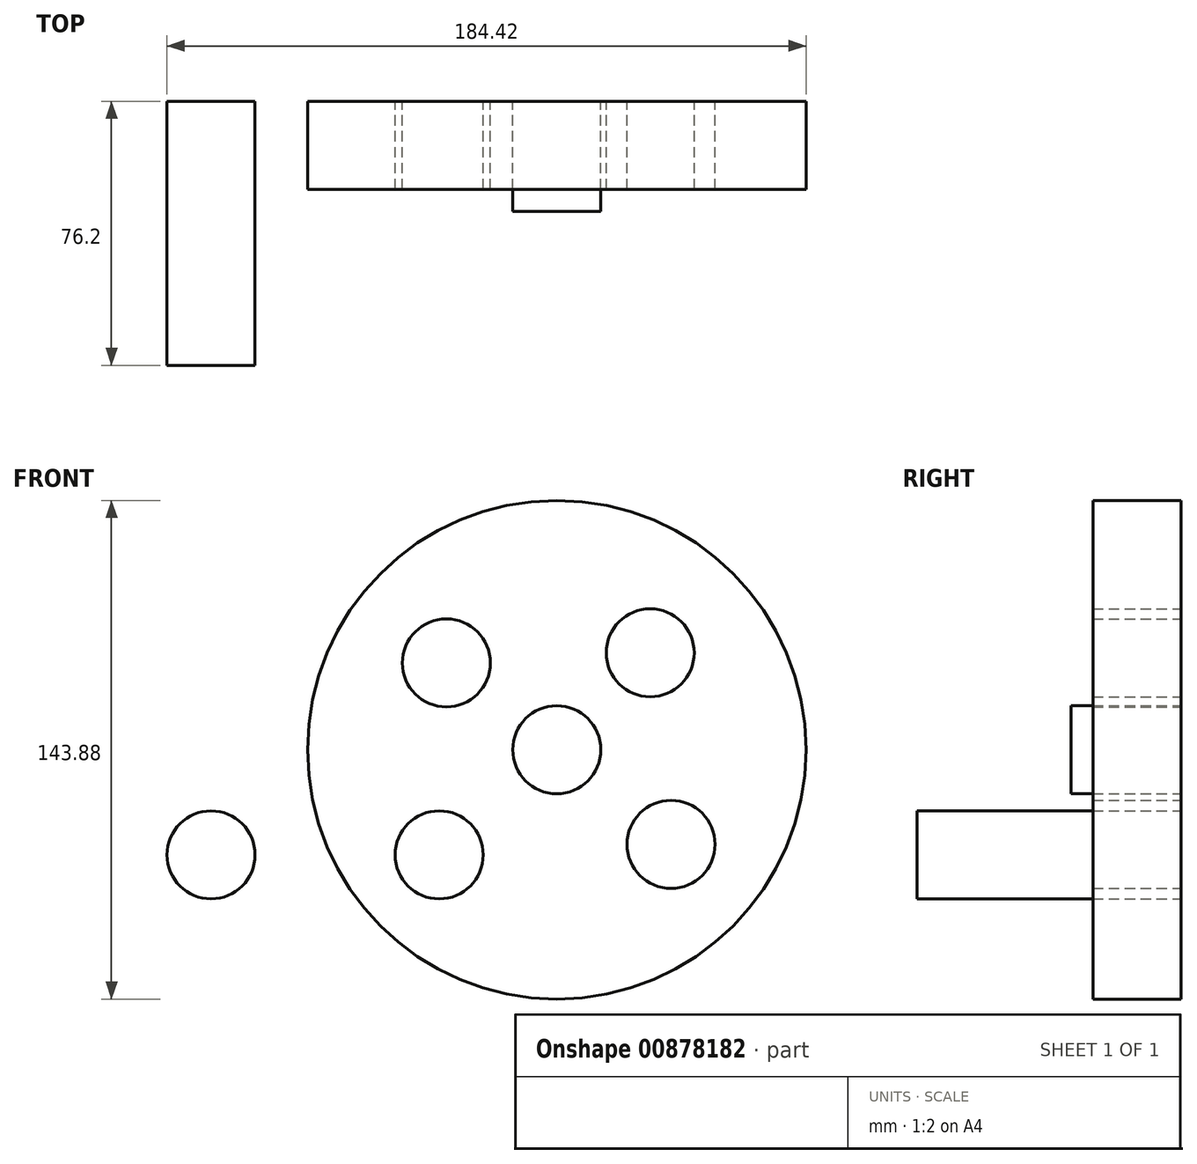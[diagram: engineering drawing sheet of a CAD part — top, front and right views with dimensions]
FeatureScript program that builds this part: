
annotation { "Feature Type Name" : "Feature", "Feature Type Description" : "" }
export const myFeature = defineFeature(function(context is Context, id is Id, definition is map)
    precondition{}
    {
        {
            var Q0;
            Q0=qCreatedBy(makeId("Front.planeOp"),FACE);
            var sketch = newSketch(context, id + "F0", { "sketchPlane" : qUnion([Q0])});
            skCircle(sketch, "E0", {"center": v(0, 0) * mm, "radius": 71.94 * mm});
            skCircle(sketch, "E1", {"center": v(0, 0) * mm, "radius": 12.7 * mm});
            skCircle(sketch, "E2", {"center": v(-31.85, 25.05) * mm, "radius": 12.7 * mm});
            skCircle(sketch, "E3", {"center": v(33, -27.31) * mm, "radius": 12.7 * mm});
            skCircle(sketch, "E4", {"center": v(30.88, 475.95) * mm, "radius": 71.94 * mm});
            skCircle(sketch, "E5", {"center": v(-99.78, -30.34) * mm, "radius": 12.7 * mm});
            skCircle(sketch, "E6", {"center": v(26.97, 27.97) * mm, "radius": 12.7 * mm});
            skCircle(sketch, "E7", {"center": v(-33.93, -30.34) * mm, "radius": 12.7 * mm});
            skPoint(sketch, "E8", {"position": v(0, 478.81) * mm});
            skPoint(sketch, "E9", {"position": v(66.36, 478.81) * mm});
            skPoint(sketch, "E10", {"position": v(40.8, 508.23) * mm});
            skPoint(sketch, "E11", {"position": v(30.88, 449.07) * mm});
            skSolve(sketch);
        }
        {
            var Q0;
            Q0=makeQuery(id+"F0.imprint","IMPRINT",FACE,{"disambiguationData":[TD([[makeQuery(id+"F0.imprint","IMPRINT",EDGE,{"derivedFrom":sQuery(id+"F0.wireOp",EDGE,"E1")}),1.0]])]});
            var Q1;
            Q1=makeQuery(id+"F0.imprint","IMPRINT",FACE,{"disambiguationData":[TD([[makeQuery(id+"F0.imprint","IMPRINT",EDGE,{"derivedFrom":sQuery(id+"F0.wireOp",EDGE,"E0")}),1.0]])]});
            extrude(context, id + "F1", {"entities" : qUnion([Q0, Q1]), "depth" : 25.4 * mm, "offsetDistance" : 25.4 * mm});
        }
        {
            var Q0;
            Q0 = qConstructionFilter(qBodyType(qCreatedBy(id + "F0" ,EDGE), BodyType.WIRE), ConstructionObject.NO);
            extrude(context, id + "F2", {"bodyType" : ToolBodyType.SURFACE, "surfaceEntities" : qUnion([Q0]), "depth" : 25.4 * mm, "offsetDistance" : 25.4 * mm});
        }
        {
            var Q0;
            Q0=makeQuery(id+"F0.imprint","IMPRINT",FACE,{"disambiguationData":[TD([[makeQuery(id+"F0.imprint","IMPRINT",EDGE,{"derivedFrom":sQuery(id+"F0.wireOp",EDGE,"E1")}),1.0]])]});
            extrude(context, id + "F3", {"entities" : qUnion([Q0]), "depth" : 31.75 * mm, "offsetDistance" : 25.4 * mm});
        }
        {
            var Q0;
            Q0=makeQuery(id+"F0.imprint","IMPRINT",FACE,{"disambiguationData":[TD([[makeQuery(id+"F0.imprint","IMPRINT",EDGE,{"derivedFrom":sQuery(id+"F0.wireOp",EDGE,"E5")}),1.0]])]});
            extrude(context, id + "F4", {"entities" : qUnion([Q0]), "depth" : 76.2 * mm, "offsetDistance" : 25.4 * mm});
        }
    });
